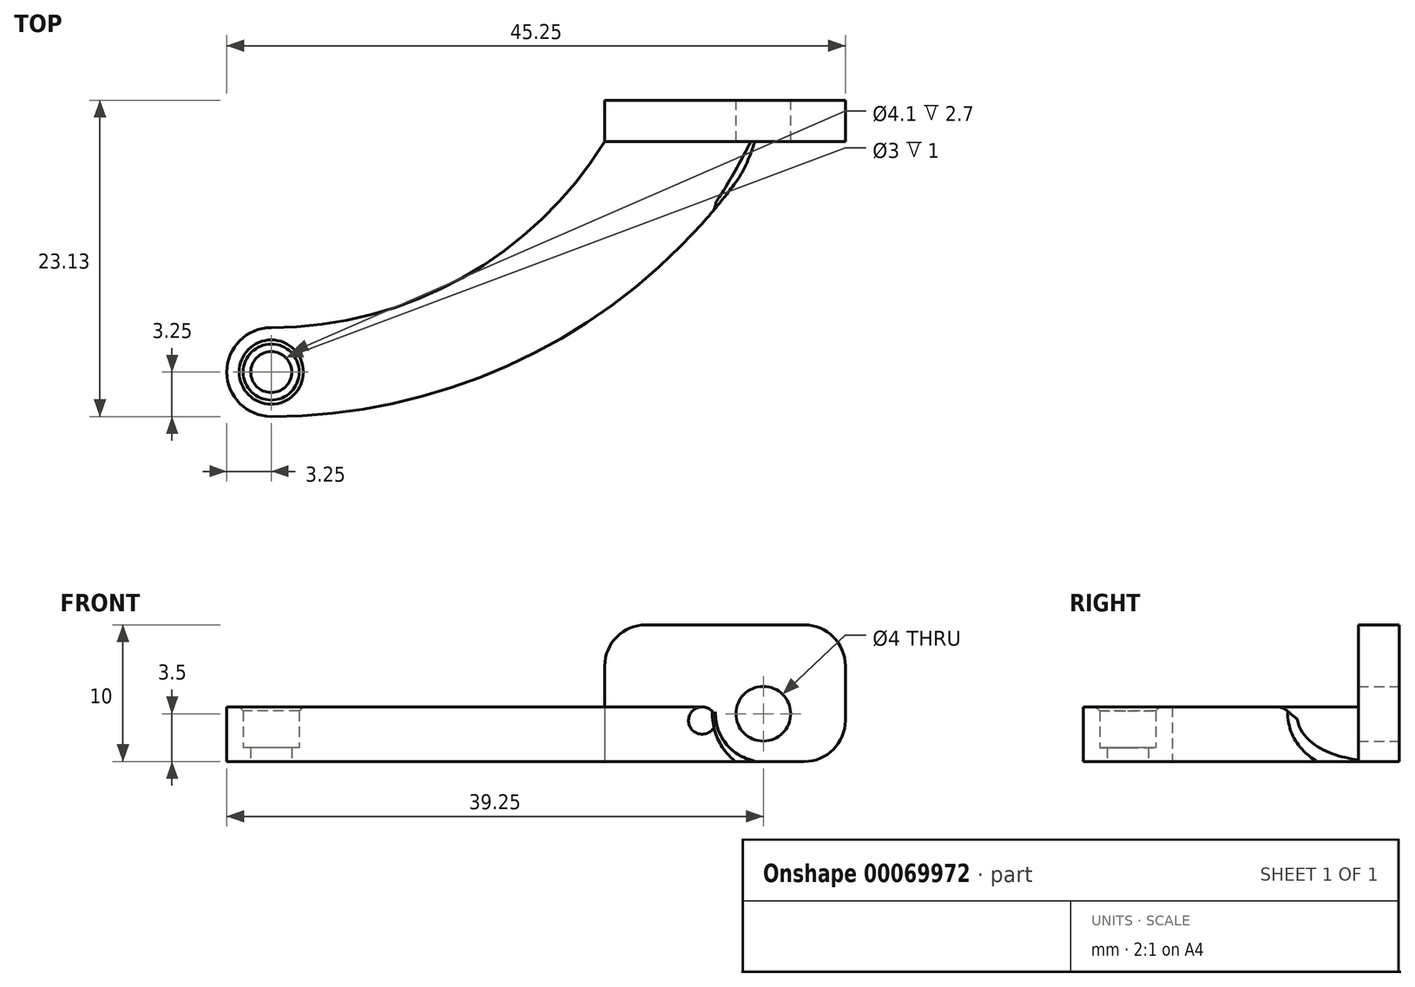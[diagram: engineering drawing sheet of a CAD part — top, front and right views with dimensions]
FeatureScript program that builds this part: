
annotation { "Feature Type Name" : "Feature", "Feature Type Description" : "" }
export const myFeature = defineFeature(function(context is Context, id is Id, definition is map)
    precondition{}
    {
        {
            var Q0;
            Q0=qCreatedBy(makeId("Top.planeOp"),FACE);
            var sketch = newSketch(context, id + "F0", { "sketchPlane" : qUnion([Q0])});
            skCircle(sketch, "E0", {"center": v(0, 0) * mm, "radius": 2.05 * mm});
            skLineSegment(sketch, "E1", {"start": v(-11.02, 19.88) * mm, "end": v(42, 19.88) * mm, "construction": true});
            skCircle(sketch, "E2", {"center": v(0, 0) * mm, "radius": 3.25 * mm});
            skLineSegment(sketch, "E3", {"start": v(36, 33.23) * mm, "end": v(36, -7.13) * mm, "construction": true});
            skLineSegment(sketch, "E4", {"start": v(24.4, 33.23) * mm, "end": v(24.4, 16.88) * mm, "construction": true});
            skPoint(sketch, "E5", {"position": v(24.4, 19.88) * mm});
            skPoint(sketch, "E6", {"position": v(36, 19.88) * mm});
            skArc(sketch, "E7", {"start": v(0, 3.25) * mm, "mid": v(13.97, 6.89) * mm, "end": v(24.4, 16.88) * mm});
            skPoint(sketch, "E8", {"position": v(36, 16.88) * mm});
            skArc(sketch, "E9", {"start": v(0, -3.25) * mm, "mid": v(20.62, 2.12) * mm, "end": v(36, 16.88) * mm});
            skLineSegment(sketch, "E10", {"start": v(24.4, 16.88) * mm, "end": v(36, 16.88) * mm});
            skLineSegment(sketch, "E11", {"start": v(24.4, 16.88) * mm, "end": v(24.4, 19.88) * mm});
            skLineSegment(sketch, "E12", {"start": v(36, 16.88) * mm, "end": v(36, 19.88) * mm});
            skLineSegment(sketch, "E13", {"start": v(24.4, 19.88) * mm, "end": v(36, 19.88) * mm});
            skLineSegment(sketch, "E14", {"start": v(0, -3.25) * mm, "end": v(-5.9, -3.25) * mm, "construction": true});
            skLineSegment(sketch, "E15", {"start": v(36, 19.88) * mm, "end": v(42, 19.88) * mm});
            skLineSegment(sketch, "E16", {"start": v(36, 16.88) * mm, "end": v(42, 16.88) * mm});
            skLineSegment(sketch, "E17", {"start": v(42, 16.88) * mm, "end": v(42, 19.88) * mm});
            skCircle(sketch, "E18", {"center": v(0, 0) * mm, "radius": 1.5 * mm});
            skSolve(sketch);
        }
        {
            var Q0;
            {var subQ0=sQuery(id+"F0.wireOp",EDGE,"E7");Q0=makeQuery(id+"F0.imprint","IMPRINT",FACE,{"disambiguationData":[TD([[makeQuery(id+"F0.imprint","IMPRINT",EDGE,{"derivedFrom":subQ0}),-1.0]])]});}
            var Q1;
            Q1=makeQuery(id+"F0.imprint","IMPRINT",FACE,{"disambiguationData":[TD([[makeQuery(id+"F0.imprint","IMPRINT",EDGE,{"derivedFrom":sQuery(id+"F0.wireOp",EDGE,"E10")}),1.0]])]});
            var Q2;
            Q2=makeQuery(id+"F0.imprint","IMPRINT",FACE,{"disambiguationData":[TD([[makeQuery(id+"F0.imprint","IMPRINT",EDGE,{"derivedFrom":sQuery(id+"F0.wireOp",EDGE,"E12")}),-1.0]])]});
            var Q3;
            Q3=makeQuery(id+"F0.imprint","IMPRINT",FACE,{"disambiguationData":[TD([[makeQuery(id+"F0.imprint","IMPRINT",EDGE,{"derivedFrom":sQuery(id+"F0.wireOp",EDGE,"E0")}),-1.0]])]});
            extrude(context, id + "F1", {"entities" : qUnion([Q0, Q1, Q2, Q3]), "depth" : 4 * mm});
        }
        {
            var Q0;
            Q0=makeQuery(id+"F0.imprint","IMPRINT",FACE,{"disambiguationData":[TD([[makeQuery(id+"F0.imprint","IMPRINT",EDGE,{"derivedFrom":sQuery(id+"F0.wireOp",EDGE,"E10")}),1.0]])]});
            var Q1;
            Q1=makeQuery(id+"F0.imprint","IMPRINT",FACE,{"disambiguationData":[TD([[makeQuery(id+"F0.imprint","IMPRINT",EDGE,{"derivedFrom":sQuery(id+"F0.wireOp",EDGE,"E12")}),-1.0]])]});
            extrude(context, id + "F2", {"entities" : qUnion([Q0, Q1]), "operationType" : NewBodyOperationType.ADD, "depth" : 10 * mm});
        }
        {
            var Q0;
            {var subQ0=sQuery(id+"F0.wireOp",EDGE,"E15");var subQ1=sQuery(id+"F0.wireOp",EDGE,"E13");Q0=makeQuery(id+"F2.boolean.opBoolean","MERGE",FACE,{"derivedFrom":[makeQuery(id+"F1.opExtrude","SWEPT_FACE",FACE,{"disambiguationData":[OSD([subQ1,subQ0])]}),makeQuery(id+"F2.opExtrude","SWEPT_FACE",FACE,{"disambiguationData":[OSD([subQ1,subQ0])]})]});}
            var sketch = newSketch(context, id + "F3", { "sketchPlane" : qUnion([Q0])});
            skCircle(sketch, "E19", {"center": v(-36, 3.5) * mm, "radius": 2 * mm});
            skSolve(sketch);
        }
        {
            var Q0;
            Q0=makeQuery(id+"F3.imprint","IMPRINT",FACE,{"disambiguationData":[TD([[makeQuery(id+"F3.imprint","IMPRINT",EDGE,{"derivedFrom":sQuery(id+"F3.wireOp",EDGE,"E19")}),1.0]])]});
            extrude(context, id + "F4", {"entities" : qUnion([Q0]), "operationType" : NewBodyOperationType.REMOVE, "endBound" : BoundingType.THROUGH_ALL, "oppositeDirection" : true, "depth" : 25 * mm});
        }
        {
            var Q0;
            {var subQ0=sQuery(id+"F0.wireOp",EDGE,"E16");Q0=makeQuery(id+"F2.boolean.opBoolean","MERGE",FACE,{"derivedFrom":[makeQuery(id+"F1.opExtrude","SWEPT_FACE",FACE,{"disambiguationData":[OSD([subQ0])]}),makeQuery(id+"F2.opExtrude","SWEPT_FACE",FACE,{"disambiguationData":[OSD([sQuery(id+"F0.wireOp",EDGE,"E10"),subQ0])]})]});}
            var sketch = newSketch(context, id + "F5", { "sketchPlane" : qUnion([Q0])});
            skCircle(sketch, "E20", {"center": v(36, 3.5) * mm, "radius": 3.5 * mm});
            skSolve(sketch);
        }
        {
            var Q0;
            Q0=qSketchRegion(id+"F5",true);
            extrude(context, id + "F6", {"entities" : qUnion([Q0]), "operationType" : NewBodyOperationType.REMOVE, "endBound" : BoundingType.THROUGH_ALL, "depth" : 25 * mm});
        }
        {
            var Q0;
            Q0=makeQuery(id+"F6.boolean.opBoolean","INTERSECT",EDGE,{"derivedFrom":[makeQuery(id+"F1.opExtrude","CAP_FACE",FACE,{"disambiguationData":[OSD([sQuery(id+"F0.wireOp",EDGE,"E0"),sQuery(id+"F0.wireOp",EDGE,"E2"),sQuery(id+"F0.wireOp",EDGE,"E7"),sQuery(id+"F0.wireOp",EDGE,"E9"),sQuery(id+"F0.wireOp",EDGE,"E11"),sQuery(id+"F0.wireOp",EDGE,"E13"),sQuery(id+"F0.wireOp",EDGE,"E15"),sQuery(id+"F0.wireOp",EDGE,"E16"),sQuery(id+"F0.wireOp",EDGE,"E17")])],"isStart":false}),makeQuery(id+"F6.opExtrude","SWEPT_FACE",FACE,{"disambiguationData":[OSD([sQuery(id+"F5.wireOp",EDGE,"E20")])]})]});
            var Q1;
            Q1=makeQuery(id+"F6.boolean.opBoolean","INTERSECT",EDGE,{"derivedFrom":[makeQuery(id+"F1.opExtrude","SWEPT_FACE",FACE,{"disambiguationData":[OSD([sQuery(id+"F0.wireOp",EDGE,"E9")])]}),makeQuery(id+"F6.opExtrude","SWEPT_FACE",FACE,{"disambiguationData":[OSD([sQuery(id+"F5.wireOp",EDGE,"E20")])]})]});
            fillet(context, id + "F7", {"entities" : qUnion([Q0, Q1]), "radius" : 1 * mm, "tangentPropagation" : true, "allowEdgeOverflow" : false});
        }
        {
            var Q0;
            Q0=makeQuery(id+"F2.opExtrude","CAP_EDGE",EDGE,{"disambiguationData":[OSD([sQuery(id+"F0.wireOp",EDGE,"E17")])],"isStart":false});
            var Q1;
            Q1=makeQuery(id+"F2.opExtrude","CAP_EDGE",EDGE,{"disambiguationData":[OSD([sQuery(id+"F0.wireOp",EDGE,"E11")])],"isStart":false});
            var Q2;
            Q2=makeQuery(id+"F1.opExtrude","CAP_EDGE",EDGE,{"disambiguationData":[OSD([sQuery(id+"F0.wireOp",EDGE,"E17")])],"isStart":true});
            fillet(context, id + "F8", {"entities" : qUnion([Q0, Q1, Q2]), "radius" : 3 * mm, "tangentPropagation" : true, "allowEdgeOverflow" : false});
        }
        {
            var Q0;
            Q0=makeQuery(id+"F1.opExtrude","CAP_EDGE",EDGE,{"disambiguationData":[OSD([sQuery(id+"F0.wireOp",EDGE,"E0")])],"isStart":false});
            chamfer(context, id + "F9", {"entities" : qUnion([Q0]), "width" : 0.3 * mm, "tangentPropagation" : true});
        }
        {
            var Q0;
            Q0=makeQuery(id+"F0.imprint","IMPRINT",FACE,{"disambiguationData":[TD([[makeQuery(id+"F0.imprint","IMPRINT",EDGE,{"derivedFrom":sQuery(id+"F0.wireOp",EDGE,"E0")}),1.0]])]});
            extrude(context, id + "F10", {"entities" : qUnion([Q0]), "operationType" : NewBodyOperationType.ADD, "depth" : 1 * mm});
        }
    });
